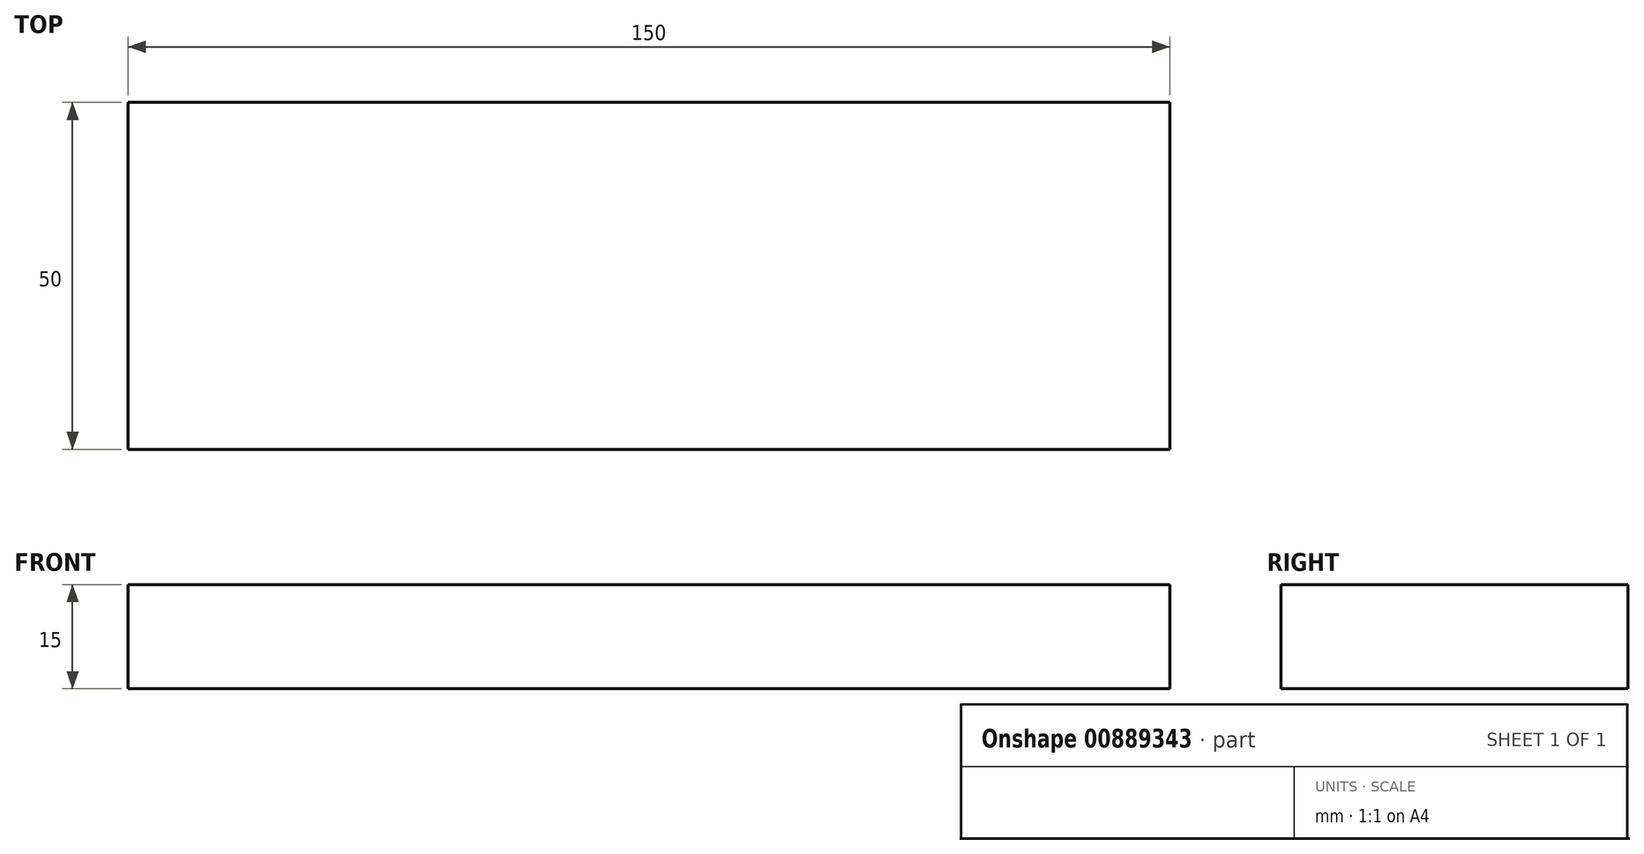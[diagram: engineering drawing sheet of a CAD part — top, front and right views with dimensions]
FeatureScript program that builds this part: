
annotation { "Feature Type Name" : "Feature", "Feature Type Description" : "" }
export const myFeature = defineFeature(function(context is Context, id is Id, definition is map)
    precondition{}
    {
        {
            var Q0;
            Q0=qCreatedBy(makeId("Top.planeOp"),FACE);
            var sketch = newSketch(context, id + "F0", { "sketchPlane" : qUnion([Q0])});
            skLineSegment(sketch, "E0.bottom", {"start": v(-98.2, 40.08) * mm, "end": v(51.8, 40.08) * mm});
            skLineSegment(sketch, "E0.top", {"start": v(-98.2, -9.92) * mm, "end": v(51.8, -9.92) * mm});
            skLineSegment(sketch, "E0.left", {"start": v(-98.2, 40.08) * mm, "end": v(-98.2, -9.92) * mm});
            skLineSegment(sketch, "E0.right", {"start": v(51.8, 40.08) * mm, "end": v(51.8, -9.92) * mm});
            skSolve(sketch);
        }
        {
            var Q0;
            Q0=makeQuery(id+"F0.imprint","IMPRINT",FACE,{"disambiguationData":[TD([[makeQuery(id+"F0.imprint","IMPRINT",EDGE,{"derivedFrom":sQuery(id+"F0.wireOp",EDGE,"E0.bottom")}),-1.0]])]});
            var sketch = newSketch(context, id + "F1", { "sketchPlane" : qUnion([Q0])});
            skSolve(sketch);
        }
        {
            var Q0;
            Q0=makeQuery(id+"F1.imprint","IMPRINT",FACE,{"disambiguationData":[TD([[makeQuery(id+"F1.imprint","IMPRINT",EDGE,{"derivedFrom":makeQuery(id+"F0.imprint","IMPRINT",EDGE,{"derivedFrom":sQuery(id+"F0.wireOp",EDGE,"E0.bottom")})}),-1.0]])]});
            extrude(context, id + "F2", {"entities" : qUnion([Q0]), "depth" : 15 * mm, "offsetDistance" : 25 * mm});
        }
    });
